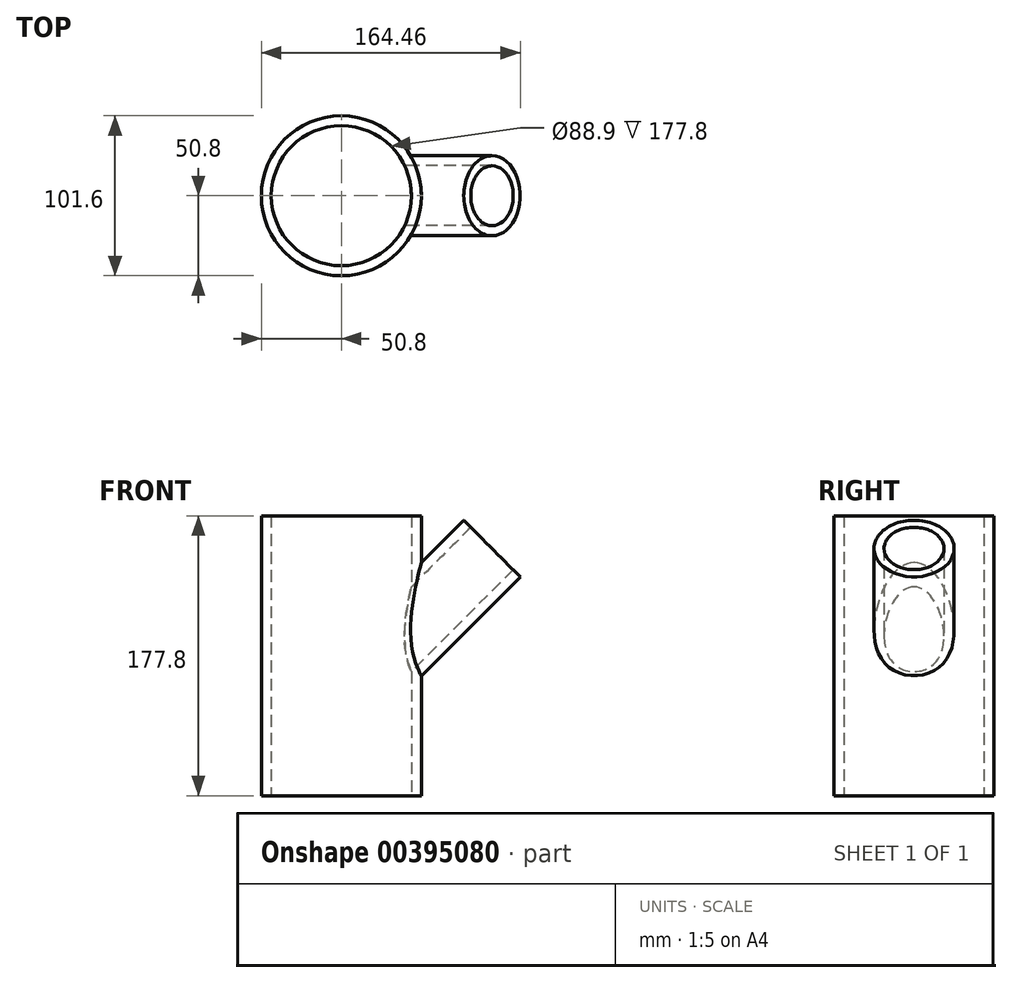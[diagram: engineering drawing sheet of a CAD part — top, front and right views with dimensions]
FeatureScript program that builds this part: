
annotation { "Feature Type Name" : "Feature", "Feature Type Description" : "" }
export const myFeature = defineFeature(function(context is Context, id is Id, definition is map)
    precondition{}
    {
        {
            var Q0;
            Q0=qCreatedBy(makeId("Front.planeOp"),FACE);
            var sketch = newSketch(context, id + "F0", { "sketchPlane" : qUnion([Q0])});
            skLineSegment(sketch, "E0", {"start": v(0, 0) * mm, "end": v(0, 177.8) * mm});
            skLineSegment(sketch, "E1", {"start": v(0, 177.8) * mm, "end": v(50.8, 177.8) * mm});
            skLineSegment(sketch, "E2", {"start": v(50.8, 177.8) * mm, "end": v(50.8, 0) * mm});
            skLineSegment(sketch, "E3", {"start": v(50.8, 0) * mm, "end": v(0, 0) * mm});
            skSolve(sketch);
        }
        {
            var Q0;
            Q0 = qSketchRegion(id + "F0", true);
            var Q1;
            Q1=sQuery(id+"F0.wireOp",EDGE,"E0");
            revolve(context, id + "F1", {"entities" : qUnion([Q0]), "axis" : qUnion([Q1]), "revolveType" : RevolveType.FULL});
        }
        {
            var Q0;
            Q0=qCreatedBy(makeId("Front.planeOp"),FACE);
            var sketch = newSketch(context, id + "F2", { "sketchPlane" : qUnion([Q0])});
            skLineSegment(sketch, "E4", {"start": v(0, 61.32) * mm, "end": v(95.7, 157.02) * mm});
            skLineSegment(sketch, "E5", {"start": v(95.7, 157.02) * mm, "end": v(113.66, 139.06) * mm});
            skLineSegment(sketch, "E6", {"start": v(113.66, 139.06) * mm, "end": v(0, 25.4) * mm});
            skLineSegment(sketch, "E7", {"start": v(0, 25.4) * mm, "end": v(0, 61.32) * mm});
            skPoint(sketch, "E8", {"position": v(50.8, 76.2) * mm});
            skSolve(sketch);
        }
        {
            var Q0;
            Q0 = qSketchRegion(id + "F2", true);
            var Q1;
            Q1=sQuery(id+"F2.wireOp",EDGE,"E4");
            revolve(context, id + "F3", {"operationType" : NewBodyOperationType.ADD, "entities" : qUnion([Q0]), "axis" : qUnion([Q1]), "revolveType" : RevolveType.FULL});
        }
        {
            var Q0;
            Q0=makeQuery(id+"F1.opRevolve","SWEPT_FACE",FACE,{"disambiguationData":[OSD([sQuery(id+"F0.wireOp",EDGE,"E1")])]});
            var Q1;
            Q1=makeQuery(id+"F3.opRevolve","SWEPT_FACE",FACE,{"disambiguationData":[OSD([sQuery(id+"F2.wireOp",EDGE,"E5")])]});
            var Q2;
            Q2=makeQuery(id+"F1.opRevolve","SWEPT_FACE",FACE,{"disambiguationData":[OSD([sQuery(id+"F0.wireOp",EDGE,"E3")])]});
            shell(context, id + "F4", {"entities" : qUnion([Q0, Q1, Q2]), "thickness" : 6.35 * mm});
        }
    });
